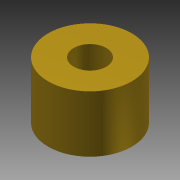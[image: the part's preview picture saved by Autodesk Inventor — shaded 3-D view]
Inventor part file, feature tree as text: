
AUTODESK INVENTOR PART (.ipt)
format: ipt  version: 2015 (Build 190159000, 159)  size: 82,432 bytes
history: native  units: in
note: dims shown in document units (in); Inventor stores cm internally (conversion verified against a paired STEP export)
features: other x2, sketch x1, imported_body x1
ambient origin geometry x8: Origin, YZ Plane, XZ Plane, XY Plane, X Axis, Y Axis, Z Axis, Center Point
bodies: Body1 (feature_tree)
feature tree (4):
  other  "Boss-Extrude1"
  other  "shaft.ipt1"
  sketch  "Sketch1"
  imported_body  "Base1"
